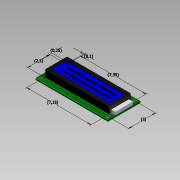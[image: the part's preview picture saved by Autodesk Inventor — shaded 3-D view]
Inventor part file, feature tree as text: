
AUTODESK INVENTOR PART (.ipt)
format: ipt  version: 2015 SP1 (Build 190203100, 203)  size: 193,024 bytes
history: native  units: in
note: dims shown in document units (in); Inventor stores cm internally (conversion verified against a paired STEP export)
features: other x2, sketch x2, imported_body x1
ambient origin geometry x8: Origin, YZ Plane, XZ Plane, XY Plane, X Axis, Y Axis, Z Axis, Center Point
bodies: Body1 (feature_tree)
feature tree (5):
  other  "Boss-Extrude5"
  other  "LCD 16x21"
  sketch  "Sketch1"  dims[d0=2.8937in]
  sketch  "Sketch2"  dims[d1=1.1811in d2=2.815in d3=0.9843in d4=0.0394in d5=0.0984in]
  imported_body  "Base1"
